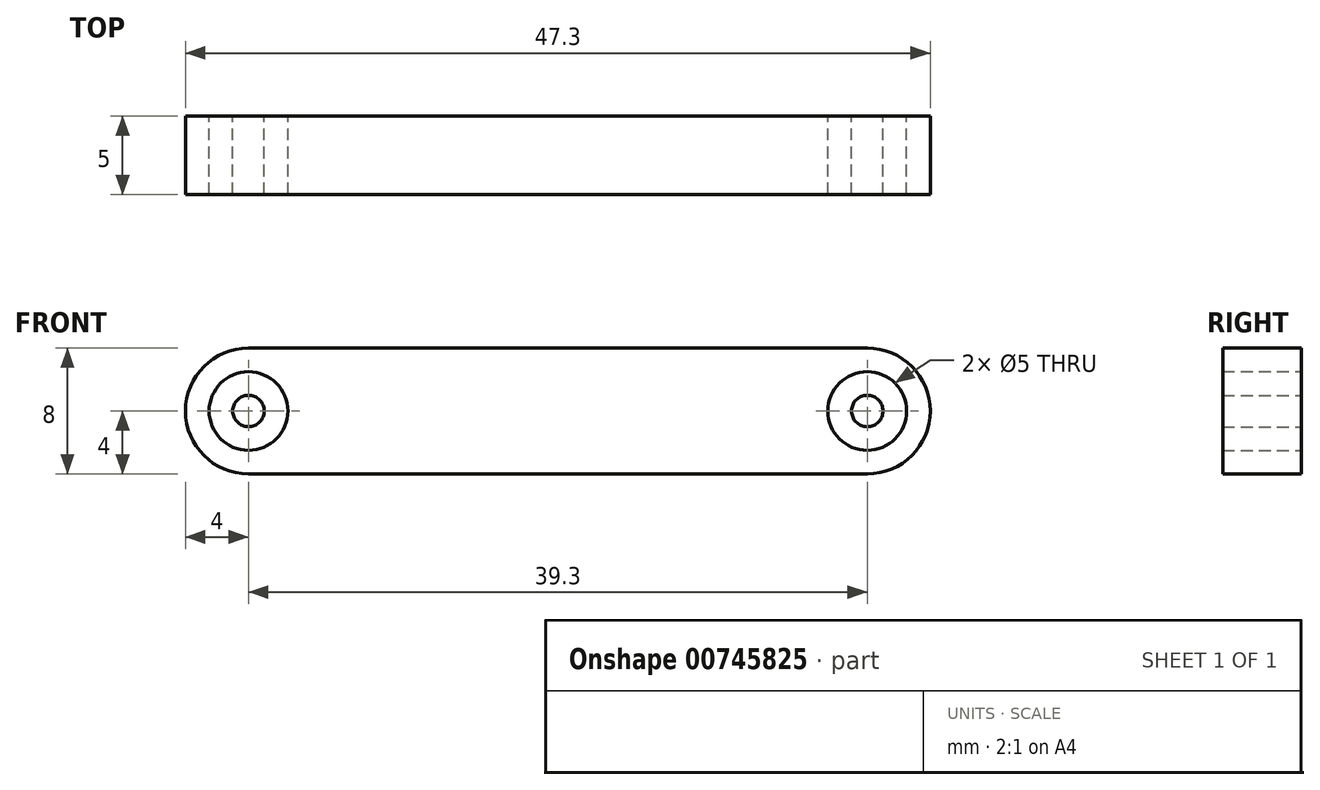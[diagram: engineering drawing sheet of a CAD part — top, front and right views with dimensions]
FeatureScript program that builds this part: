
annotation { "Feature Type Name" : "Feature", "Feature Type Description" : "" }
export const myFeature = defineFeature(function(context is Context, id is Id, definition is map)
    precondition{}
    {
        {
            var Q0;
            Q0=qCreatedBy(makeId("Front.planeOp"),FACE);
            var sketch = newSketch(context, id + "F0", { "sketchPlane" : qUnion([Q0])});
            skArc(sketch, "E0", {"start": v(0, 4) * mm, "mid": v(-4, 0) * mm, "end": v(0, -4) * mm});
            skCircle(sketch, "E1", {"center": v(0, 0) * mm, "radius": 2.5 * mm});
            skCircle(sketch, "E2", {"center": v(0, 0) * mm, "radius": 1 * mm});
            skArc(sketch, "E3", {"start": v(39.3, -4) * mm, "mid": v(43.3, 0) * mm, "end": v(39.3, 4) * mm});
            skCircle(sketch, "E4", {"center": v(39.3, 0) * mm, "radius": 2.5 * mm});
            skCircle(sketch, "E5", {"center": v(39.3, 0) * mm, "radius": 1 * mm});
            skLineSegment(sketch, "E6", {"start": v(0, 4) * mm, "end": v(39.3, 4) * mm});
            skLineSegment(sketch, "E7", {"start": v(0, -4) * mm, "end": v(39.3, -4) * mm});
            skSolve(sketch);
        }
        {
            var Q0;
            Q0 = qSketchRegion(id + "F0", true);
            var Q1;
            Q1=makeQuery(id+"F0.imprint","IMPRINT",FACE,{"disambiguationData":[TD([[makeQuery(id+"F0.imprint","IMPRINT",EDGE,{"derivedFrom":sQuery(id+"F0.wireOp",EDGE,"E2")}),1.0]])]});
            var Q2;
            Q2=makeQuery(id+"F0.imprint","IMPRINT",FACE,{"disambiguationData":[TD([[makeQuery(id+"F0.imprint","IMPRINT",EDGE,{"derivedFrom":sQuery(id+"F0.wireOp",EDGE,"E5")}),1.0]])]});
            extrude(context, id + "F1", {"entities" : qUnion([Q0, Q1, Q2]), "depth" : 5 * mm, "offsetDistance" : 25.4 * mm});
        }
    });
